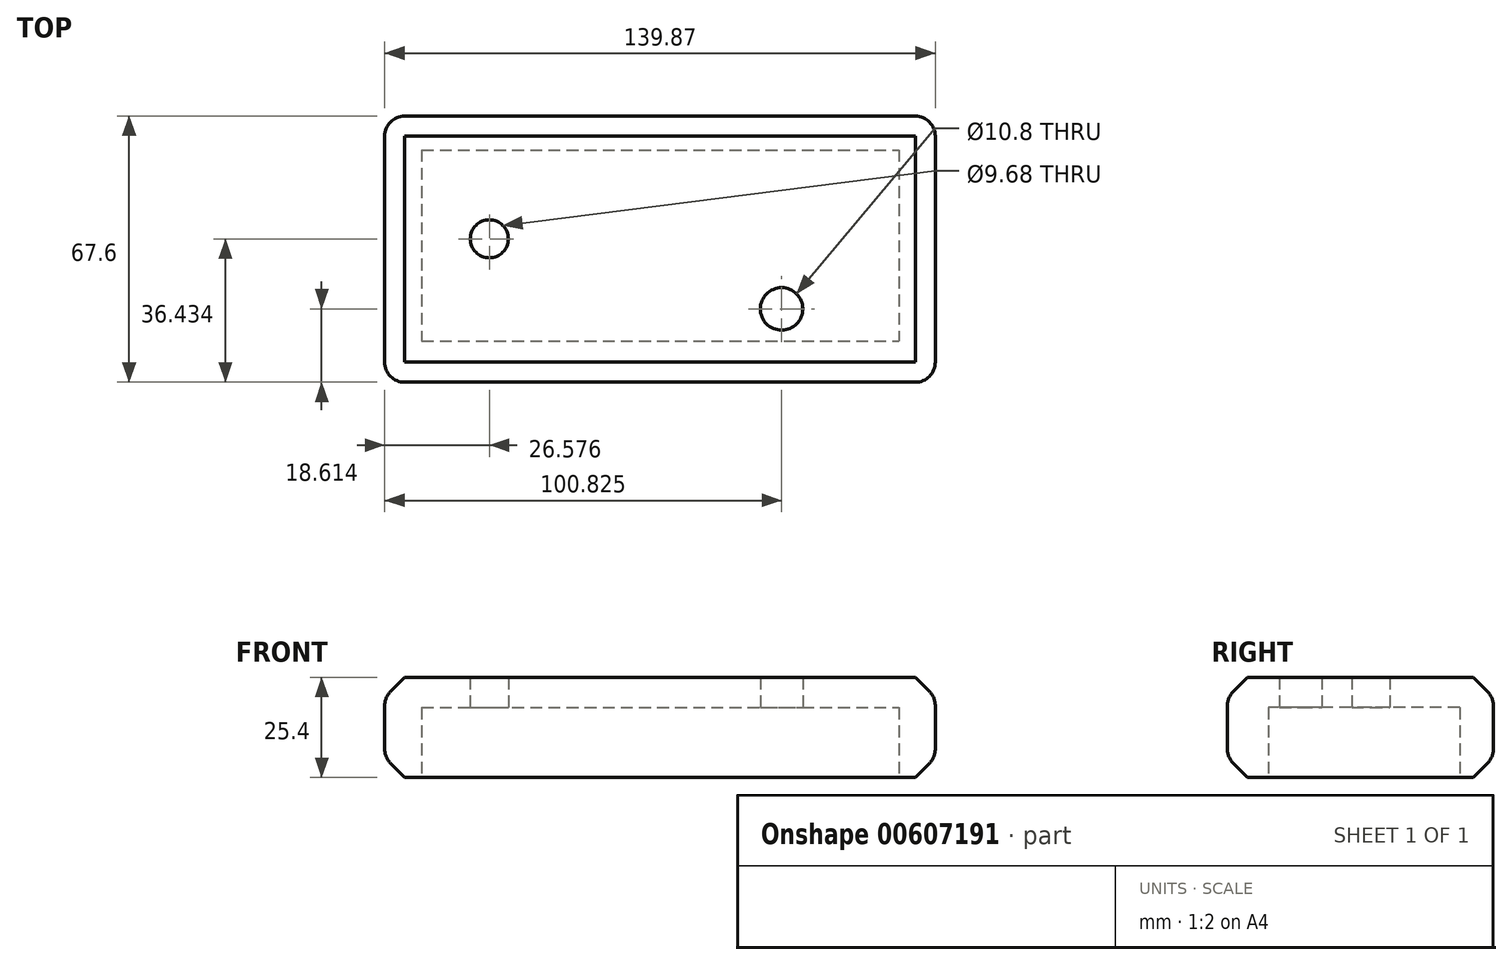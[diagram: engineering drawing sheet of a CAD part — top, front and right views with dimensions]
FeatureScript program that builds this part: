
annotation { "Feature Type Name" : "Feature", "Feature Type Description" : "" }
export const myFeature = defineFeature(function(context is Context, id is Id, definition is map)
    precondition{}
    {
        {
            var Q0;
            Q0=qCreatedBy(makeId("Top.planeOp"),FACE);
            var sketch = newSketch(context, id + "F0", { "sketchPlane" : qUnion([Q0])});
            skLineSegment(sketch, "E0", {"start": v(0, 0) * mm, "end": v(-70.52, 0) * mm});
            skLineSegment(sketch, "E1.bottom", {"start": v(-70.52, 0) * mm, "end": v(69.35, 0) * mm});
            skLineSegment(sketch, "E1.top", {"start": v(-70.52, 67.6) * mm, "end": v(69.35, 67.6) * mm});
            skLineSegment(sketch, "E1.left", {"start": v(-70.52, 0) * mm, "end": v(-70.52, 67.6) * mm});
            skLineSegment(sketch, "E1.right", {"start": v(69.35, 0) * mm, "end": v(69.35, 67.6) * mm});
            skSolve(sketch);
        }
        {
            var Q0;
            Q0=makeQuery(id+"F0.imprint","IMPRINT",FACE,{"disambiguationData":[TD([[makeQuery(id+"F0.imprint","IMPRINT",EDGE,{"derivedFrom":sQuery(id+"F0.wireOp",EDGE,"E1.top")}),-1.0]])]});
            extrude(context, id + "F1", {"entities" : qUnion([Q0]), "depth" : 25.4 * mm, "offsetDistance" : 25.4 * mm});
        }
        {
            var Q0;
            Q0=makeQuery(id+"F1.opExtrude","SWEPT_EDGE",EDGE,{"disambiguationData":[OSD([sQuery(id+"F0.wireOp",EDGE,"E1.bottom"),sQuery(id+"F0.wireOp",EDGE,"E1.right")])]});
            var Q1;
            Q1=makeQuery(id+"F1.opExtrude","SWEPT_EDGE",EDGE,{"disambiguationData":[OSD([sQuery(id+"F0.wireOp",EDGE,"E1.top"),sQuery(id+"F0.wireOp",EDGE,"E1.right")])]});
            var Q2;
            Q2=makeQuery(id+"F1.opExtrude","SWEPT_EDGE",EDGE,{"disambiguationData":[OSD([sQuery(id+"F0.wireOp",EDGE,"E1.top"),sQuery(id+"F0.wireOp",EDGE,"E1.left")])]});
            var Q3;
            Q3=makeQuery(id+"F1.opExtrude","SWEPT_EDGE",EDGE,{"disambiguationData":[OSD([sQuery(id+"F0.wireOp",EDGE,"E1.bottom"),sQuery(id+"F0.wireOp",EDGE,"E1.left")])]});
            fillet(context, id + "F2", {"entities" : qUnion([Q0, Q1, Q2, Q3]), "radius" : 5.08 * mm, "tangentPropagation" : true, "allowEdgeOverflow" : false});
        }
        {
            var Q0;
            Q0=makeQuery(id+"F1.opExtrude","CAP_FACE",FACE,{"disambiguationData":[OSD([sQuery(id+"F0.wireOp",EDGE,"E1.bottom"),sQuery(id+"F0.wireOp",EDGE,"E1.top"),sQuery(id+"F0.wireOp",EDGE,"E1.left"),sQuery(id+"F0.wireOp",EDGE,"E1.right")])],"isStart":true});
            var sketch = newSketch(context, id + "F3", { "sketchPlane" : qUnion([Q0])});
            skLineSegment(sketch, "E2.bottom", {"start": v(-61.12, -59.02) * mm, "end": v(60.08, -59.02) * mm});
            skLineSegment(sketch, "E2.top", {"start": v(-61.12, -10.48) * mm, "end": v(60.08, -10.48) * mm});
            skLineSegment(sketch, "E2.left", {"start": v(-61.12, -59.02) * mm, "end": v(-61.12, -10.48) * mm});
            skLineSegment(sketch, "E2.right", {"start": v(60.08, -59.02) * mm, "end": v(60.08, -10.48) * mm});
            skSolve(sketch);
        }
        {
            var Q0;
            Q0=makeQuery(id+"F3.imprint","IMPRINT",FACE,{"disambiguationData":[TD([[makeQuery(id+"F3.imprint","IMPRINT",EDGE,{"derivedFrom":sQuery(id+"F3.wireOp",EDGE,"E2.bottom")}),1.0]])]});
            extrude(context, id + "F4", {"entities" : qUnion([Q0]), "operationType" : NewBodyOperationType.REMOVE, "oppositeDirection" : true, "depth" : 17.78 * mm, "offsetDistance" : 25.4 * mm});
        }
        {
            var Q0;
            Q0=makeQuery(id+"F4.boolean.opBoolean","COPY",FACE,{"derivedFrom":makeQuery(id+"F4.opExtrude","CAP_FACE",FACE,{"disambiguationData":[OSD([sQuery(id+"F3.wireOp",EDGE,"E2.bottom"),sQuery(id+"F3.wireOp",EDGE,"E2.top"),sQuery(id+"F3.wireOp",EDGE,"E2.left"),sQuery(id+"F3.wireOp",EDGE,"E2.right")])],"isStart":false})});
            var sketch = newSketch(context, id + "F5", { "sketchPlane" : qUnion([Q0])});
            skCircle(sketch, "E3", {"center": v(-43.94, -36.43) * mm, "radius": 4.84 * mm});
            skCircle(sketch, "E4", {"center": v(30.3, -18.61) * mm, "radius": 5.4 * mm});
            skSolve(sketch);
        }
        {
            var Q0;
            Q0 = qSketchRegion(id + "F5", true);
            extrude(context, id + "F6", {"entities" : qUnion([Q0]), "operationType" : NewBodyOperationType.REMOVE, "oppositeDirection" : true, "depth" : 25.4 * mm, "offsetDistance" : 25.4 * mm});
        }
        {
            var Q0;
            Q0=makeQuery(id+"F1.opExtrude","CAP_EDGE",EDGE,{"disambiguationData":[OSD([sQuery(id+"F0.wireOp",EDGE,"E1.bottom")])],"isStart":true});
            var Q1;
            Q1=makeQuery(id+"F4.boolean.opBoolean","COPY",EDGE,{"derivedFrom":makeQuery(id+"F4.opExtrude","CAP_EDGE",EDGE,{"disambiguationData":[OSD([sQuery(id+"F3.wireOp",EDGE,"E2.top")])],"isStart":true})});
            var Q2;
            Q2=makeQuery(id+"F1.opExtrude","CAP_EDGE",EDGE,{"disambiguationData":[OSD([sQuery(id+"F0.wireOp",EDGE,"E1.bottom")])],"isStart":false});
            chamfer(context, id + "F7", {"entities" : qUnion([Q0, Q1, Q2]), "width" : 5.08 * mm, "tangentPropagation" : true});
        }
        {
            var Q0;
            {var subQ0=sQuery(id+"F0.wireOp",EDGE,"E1.right");var subQ1=sQuery(id+"F0.wireOp",EDGE,"E1.left");var subQ2=sQuery(id+"F0.wireOp",EDGE,"E1.top");var subQ3=sQuery(id+"F0.wireOp",EDGE,"E1.bottom");Q0=makeQuery(id+"F7.opChamfer","BLEND_FACE",FACE,{"disambiguationData":[OSD([subQ3,subQ2,subQ1,subQ0]),TDD([makeQuery(id+"F2.opFillet","BLEND_EDGE",EDGE,{"blendedFrom":[makeQuery(id+"F1.opExtrude","SWEPT_EDGE",EDGE,{"disambiguationData":[OSD([subQ2,subQ0])]}),makeQuery(id+"F1.opExtrude","CAP_FACE",FACE,{"disambiguationData":[OSD([subQ3,subQ2,subQ1,subQ0])],"isStart":true})],"blendedInto":[makeQuery(id+"F1.opExtrude","CAP_FACE",FACE,{"disambiguationData":[OSD([subQ3,subQ2,subQ1,subQ0])],"isStart":true})]})])]});}
            var Q1;
            {var subQ0=sQuery(id+"F0.wireOp",EDGE,"E1.right");var subQ1=sQuery(id+"F0.wireOp",EDGE,"E1.left");var subQ2=sQuery(id+"F0.wireOp",EDGE,"E1.top");var subQ3=sQuery(id+"F0.wireOp",EDGE,"E1.bottom");Q1=makeQuery(id+"F7.opChamfer","BLEND_FACE",FACE,{"disambiguationData":[OSD([subQ3,subQ2,subQ1,subQ0]),TDD([makeQuery(id+"F2.opFillet","BLEND_EDGE",EDGE,{"blendedFrom":[makeQuery(id+"F1.opExtrude","SWEPT_EDGE",EDGE,{"disambiguationData":[OSD([subQ2,subQ0])]}),makeQuery(id+"F1.opExtrude","CAP_FACE",FACE,{"disambiguationData":[OSD([subQ3,subQ2,subQ1,subQ0])],"isStart":false})],"blendedInto":[makeQuery(id+"F1.opExtrude","CAP_FACE",FACE,{"disambiguationData":[OSD([subQ3,subQ2,subQ1,subQ0])],"isStart":false})]})])]});}
            var Q2;
            {var subQ0=sQuery(id+"F0.wireOp",EDGE,"E1.right");var subQ1=sQuery(id+"F0.wireOp",EDGE,"E1.left");var subQ2=sQuery(id+"F0.wireOp",EDGE,"E1.top");var subQ3=sQuery(id+"F0.wireOp",EDGE,"E1.bottom");Q2=makeQuery(id+"F7.opChamfer","BLEND_FACE",FACE,{"disambiguationData":[OSD([subQ3,subQ2,subQ1,subQ0]),TDD([makeQuery(id+"F2.opFillet","BLEND_EDGE",EDGE,{"blendedFrom":[makeQuery(id+"F1.opExtrude","SWEPT_EDGE",EDGE,{"disambiguationData":[OSD([subQ3,subQ0])]}),makeQuery(id+"F1.opExtrude","CAP_FACE",FACE,{"disambiguationData":[OSD([subQ3,subQ2,subQ1,subQ0])],"isStart":false})],"blendedInto":[makeQuery(id+"F1.opExtrude","CAP_FACE",FACE,{"disambiguationData":[OSD([subQ3,subQ2,subQ1,subQ0])],"isStart":false})]})])]});}
            var Q3;
            {var subQ0=sQuery(id+"F0.wireOp",EDGE,"E1.right");var subQ1=sQuery(id+"F0.wireOp",EDGE,"E1.left");var subQ2=sQuery(id+"F0.wireOp",EDGE,"E1.top");var subQ3=sQuery(id+"F0.wireOp",EDGE,"E1.bottom");Q3=makeQuery(id+"F7.opChamfer","BLEND_FACE",FACE,{"disambiguationData":[OSD([subQ3,subQ2,subQ1,subQ0]),TDD([makeQuery(id+"F2.opFillet","BLEND_EDGE",EDGE,{"blendedFrom":[makeQuery(id+"F1.opExtrude","SWEPT_EDGE",EDGE,{"disambiguationData":[OSD([subQ2,subQ1])]}),makeQuery(id+"F1.opExtrude","CAP_FACE",FACE,{"disambiguationData":[OSD([subQ3,subQ2,subQ1,subQ0])],"isStart":true})],"blendedInto":[makeQuery(id+"F1.opExtrude","CAP_FACE",FACE,{"disambiguationData":[OSD([subQ3,subQ2,subQ1,subQ0])],"isStart":true})]})])]});}
            var Q4;
            {var subQ0=sQuery(id+"F0.wireOp",EDGE,"E1.right");var subQ1=sQuery(id+"F0.wireOp",EDGE,"E1.left");var subQ2=sQuery(id+"F0.wireOp",EDGE,"E1.top");var subQ3=sQuery(id+"F0.wireOp",EDGE,"E1.bottom");Q4=makeQuery(id+"F7.opChamfer","BLEND_FACE",FACE,{"disambiguationData":[OSD([subQ3,subQ2,subQ1,subQ0]),TDD([makeQuery(id+"F2.opFillet","BLEND_EDGE",EDGE,{"blendedFrom":[makeQuery(id+"F1.opExtrude","SWEPT_EDGE",EDGE,{"disambiguationData":[OSD([subQ2,subQ1])]}),makeQuery(id+"F1.opExtrude","CAP_FACE",FACE,{"disambiguationData":[OSD([subQ3,subQ2,subQ1,subQ0])],"isStart":false})],"blendedInto":[makeQuery(id+"F1.opExtrude","CAP_FACE",FACE,{"disambiguationData":[OSD([subQ3,subQ2,subQ1,subQ0])],"isStart":false})]})])]});}
            var Q5;
            {var subQ0=sQuery(id+"F0.wireOp",EDGE,"E1.right");var subQ1=sQuery(id+"F0.wireOp",EDGE,"E1.left");var subQ2=sQuery(id+"F0.wireOp",EDGE,"E1.top");var subQ3=sQuery(id+"F0.wireOp",EDGE,"E1.bottom");Q5=makeQuery(id+"F7.opChamfer","BLEND_FACE",FACE,{"disambiguationData":[OSD([subQ3,subQ2,subQ1,subQ0]),TDD([makeQuery(id+"F2.opFillet","BLEND_EDGE",EDGE,{"blendedFrom":[makeQuery(id+"F1.opExtrude","SWEPT_EDGE",EDGE,{"disambiguationData":[OSD([subQ3,subQ1])]}),makeQuery(id+"F1.opExtrude","CAP_FACE",FACE,{"disambiguationData":[OSD([subQ3,subQ2,subQ1,subQ0])],"isStart":true})],"blendedInto":[makeQuery(id+"F1.opExtrude","CAP_FACE",FACE,{"disambiguationData":[OSD([subQ3,subQ2,subQ1,subQ0])],"isStart":true})]})])]});}
            var Q6;
            {var subQ0=sQuery(id+"F0.wireOp",EDGE,"E1.right");var subQ1=sQuery(id+"F0.wireOp",EDGE,"E1.left");var subQ2=sQuery(id+"F0.wireOp",EDGE,"E1.top");var subQ3=sQuery(id+"F0.wireOp",EDGE,"E1.bottom");Q6=makeQuery(id+"F7.opChamfer","BLEND_FACE",FACE,{"disambiguationData":[OSD([subQ3,subQ2,subQ1,subQ0]),TDD([makeQuery(id+"F2.opFillet","BLEND_EDGE",EDGE,{"blendedFrom":[makeQuery(id+"F1.opExtrude","SWEPT_EDGE",EDGE,{"disambiguationData":[OSD([subQ3,subQ1])]}),makeQuery(id+"F1.opExtrude","CAP_FACE",FACE,{"disambiguationData":[OSD([subQ3,subQ2,subQ1,subQ0])],"isStart":false})],"blendedInto":[makeQuery(id+"F1.opExtrude","CAP_FACE",FACE,{"disambiguationData":[OSD([subQ3,subQ2,subQ1,subQ0])],"isStart":false})]})])]});}
            fillet(context, id + "F8", {"entities" : qUnion([Q0, Q1, Q2, Q3, Q4, Q5, Q6]), "radius" : 5.08 * mm, "tangentPropagation" : true, "allowEdgeOverflow" : false});
        }
    });
